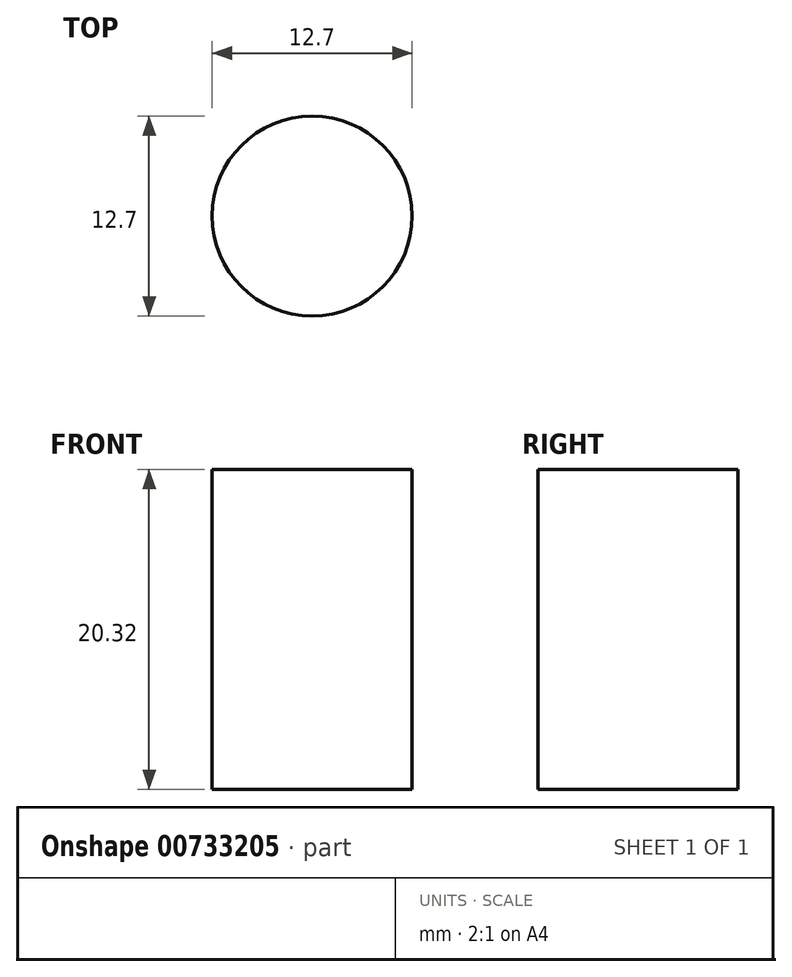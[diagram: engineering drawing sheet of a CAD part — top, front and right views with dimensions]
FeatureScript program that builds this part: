
annotation { "Feature Type Name" : "Feature", "Feature Type Description" : "" }
export const myFeature = defineFeature(function(context is Context, id is Id, definition is map)
    precondition{}
    {
        {
            var Q0;
            Q0=qCreatedBy(makeId("Top.planeOp"),FACE);
            var sketch = newSketch(context, id + "F0", { "sketchPlane" : qUnion([Q0])});
            skCircle(sketch, "E0", {"center": v(0, 0) * mm, "radius": 6.35 * mm});
            skSolve(sketch);
        }
        {
            var Q0;
            Q0=makeQuery(id+"F0.imprint","IMPRINT",FACE,{"disambiguationData":[TD([[makeQuery(id+"F0.imprint","IMPRINT",EDGE,{"derivedFrom":sQuery(id+"F0.wireOp",EDGE,"E0")}),1.0]])]});
            extrude(context, id + "F1", {"entities" : qUnion([Q0]), "depth" : 20.32 * mm, "offsetDistance" : 25.4 * mm});
        }
    });
